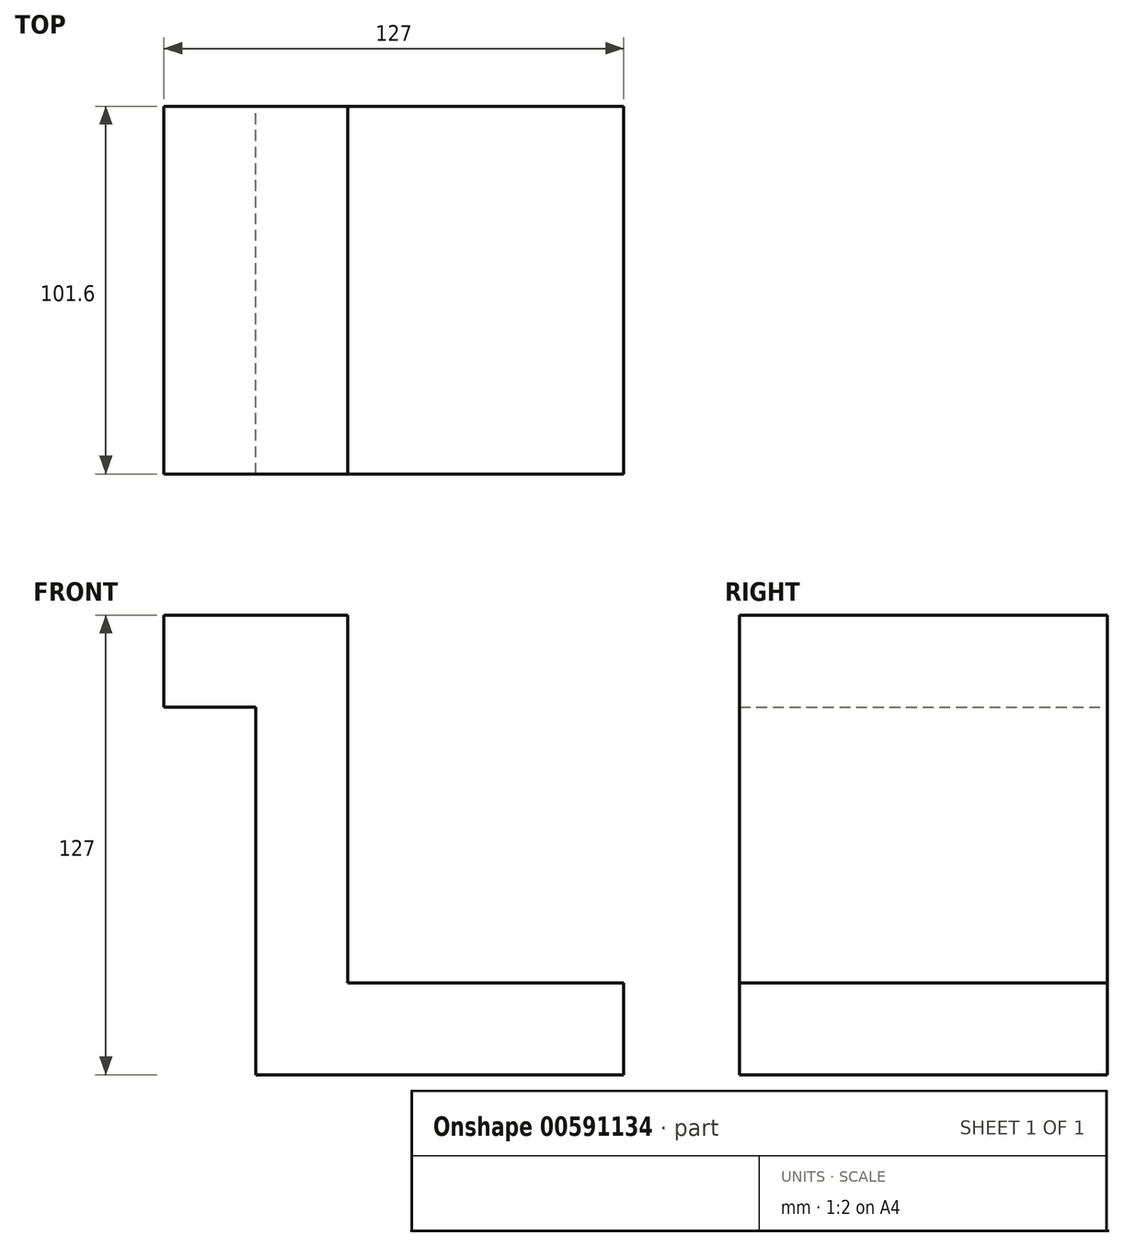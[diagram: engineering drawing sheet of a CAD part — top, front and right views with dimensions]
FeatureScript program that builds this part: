
annotation { "Feature Type Name" : "Feature", "Feature Type Description" : "" }
export const myFeature = defineFeature(function(context is Context, id is Id, definition is map)
    precondition{}
    {
        {
            var Q0;
            Q0=qCreatedBy(makeId("Front.planeOp"),FACE);
            var sketch = newSketch(context, id + "F0", { "sketchPlane" : qUnion([Q0])});
            skLineSegment(sketch, "E0", {"start": v(0, 0) * mm, "end": v(-76.2, 0) * mm});
            skLineSegment(sketch, "E1", {"start": v(-76.2, 0) * mm, "end": v(-76.2, 101.6) * mm});
            skLineSegment(sketch, "E2", {"start": v(-76.2, 101.6) * mm, "end": v(-127, 101.6) * mm});
            skLineSegment(sketch, "E3", {"start": v(-127, 101.6) * mm, "end": v(-127, 76.2) * mm});
            skLineSegment(sketch, "E4", {"start": v(-127, 76.2) * mm, "end": v(-101.6, 76.2) * mm});
            skLineSegment(sketch, "E5", {"start": v(-101.6, 76.2) * mm, "end": v(-101.6, 0) * mm});
            skLineSegment(sketch, "E6", {"start": v(-101.6, 0) * mm, "end": v(-101.6, -25.4) * mm});
            skLineSegment(sketch, "E7", {"start": v(-101.6, -25.4) * mm, "end": v(0, -25.4) * mm});
            skLineSegment(sketch, "E8", {"start": v(0, -25.4) * mm, "end": v(0, 0) * mm});
            skSolve(sketch);
        }
        {
            var Q0;
            Q0=makeQuery(id+"F0.imprint","IMPRINT",FACE,{"disambiguationData":[TD([[makeQuery(id+"F0.imprint","IMPRINT",EDGE,{"derivedFrom":sQuery(id+"F0.wireOp",EDGE,"E0")}),1.0]])]});
            extrude(context, id + "F1", {"entities" : qUnion([Q0]), "depth" : 101.6 * mm, "offsetDistance" : 25.4 * mm});
        }
    });
